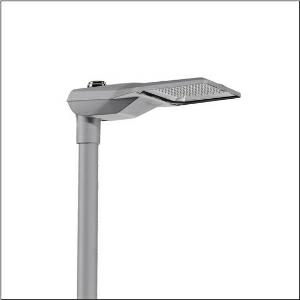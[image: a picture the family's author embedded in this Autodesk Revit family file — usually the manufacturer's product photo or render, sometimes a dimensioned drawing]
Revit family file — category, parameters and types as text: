
# Revit family: streetlight_sl_21_midi___pl52_5xe7h37n08lb_6d16
name_source: partatom
category: Lighting Fixtures
units: mm (PartAtom-declared; Revit-internal decimal feet)

## family parameters
Cut with Voids When Loaded = No
Host = Face
Light Source = No
Part Type = Normal
Room Calculation Point = No
Round Connector Dimension = Use Diameter
Shared = No

## types (1)
- --- (1 x LED, 14100 lm, 98.3 W, 3000K)
    Apparent Load = 98 VA
    CIE Flux Codes = 27 59 98 100 100
    Color Rendering = 70
    Color Temperature = 3000K
    Default Elevation = 1800 mm
    Description = Streetlight SL 21 midi, mast luminaire, primary light control with lens, of PMMA, primary optical cover: cover, of toughened safety glass, transparent, light distribution: PL52, light emission: direct distribution, primary light characteristic: asymmetric, installation type: side-entry, LED, 3G 2.5mm², High Power LED, rated luminous flux: 14.100lm, luminous efficacy: 143lm/W, light colour: 730, colour temperature: 3000K, control gear: NEMA (7pin), control: overheat protection, pre-setting: linear dimming characteristic, constant luminous flux control, time-dependent luminous flux control, flexible luminous flux parameterisation, mains connection: 220..240V, AC, 50/60Hz, connection cable pre-assembled, cable length: 10,5m, wiring characteristics: H05VV-F, start of lifetime: 98W, end of service life: 101W, reduction: 45W, luminaire housing, of diecast aluminium (EN AC-44300), powder-coated, Siteco® metallic grey (DB 702S), corrosivity category C5 mid according to DIN EN ISO 12944, multi-level sealing system, sealing non-destructively replaceable, inclination adjustable: 0°, 5°, 10°, 15°, length: 644mm, width: 335mm, height: 110mm, spigot size: 42mm (side-entry), mounting height: 4..8m, protection rating (complete): IP66, insulation class (complete): insulation class I (protective earthing), certification: CE, ENEC, ENEC+, VDE, impact resistance: IK10, permissible operating ambient temperature for outdoor applications: -40..+50°C, standard-compliant lighting for roads and squares, packaging unit: 1 piece

Light Distribution: PL52
    Height = 111 mm
    Lamp = 1 x LED
    Lamp Light Flux = 14100 lm
    Lamp Power = 98.3 W
    Lamp count = 1
    Length = 644 mm
    Luminous efficacy = 143 lm/W
    Manufacturer = Siteco
    ModVariant = No
    Model = 5XE7H37N08LB
    Number of Poles = 1
    OnlyDefault = Yes
    Power Factor = 1
    Product Name = Streetlight SL 21 midi | PL52
    Product group = mast luminaire | pylon top
    ProductGroupID = 6100
    Protection Class = Protection class I
    Protection Degree = IP 66
    RLX_Detail_Level = 1
    RLX_Emergency_Light_Flux = 0 lm
    RLX_Emergency_Type = 0
    RLX_Emergency_Type_DB = No
    RlxData = <blob elided: 36265 chars, md5=6bf1c024>
    Socket = socket
    Standby Power = 0 W
    System Light Flux = 14100 lm
    System Power = 98 W
    Type Comments = factory setting: luminous flux: 100 % | dim-lin: 254 | 1020 mA
    Type Image = l_1294377.jpg
    URL = http://relux.com
    VarID = @adj_158405
    Voltage = 0 V
    Weight = 0.00 kg
    Width = 336 mm

## geometry (parser evidence)
native form markers: Blend x4, Sweep x12
no freeform markers — native parametric forms only
